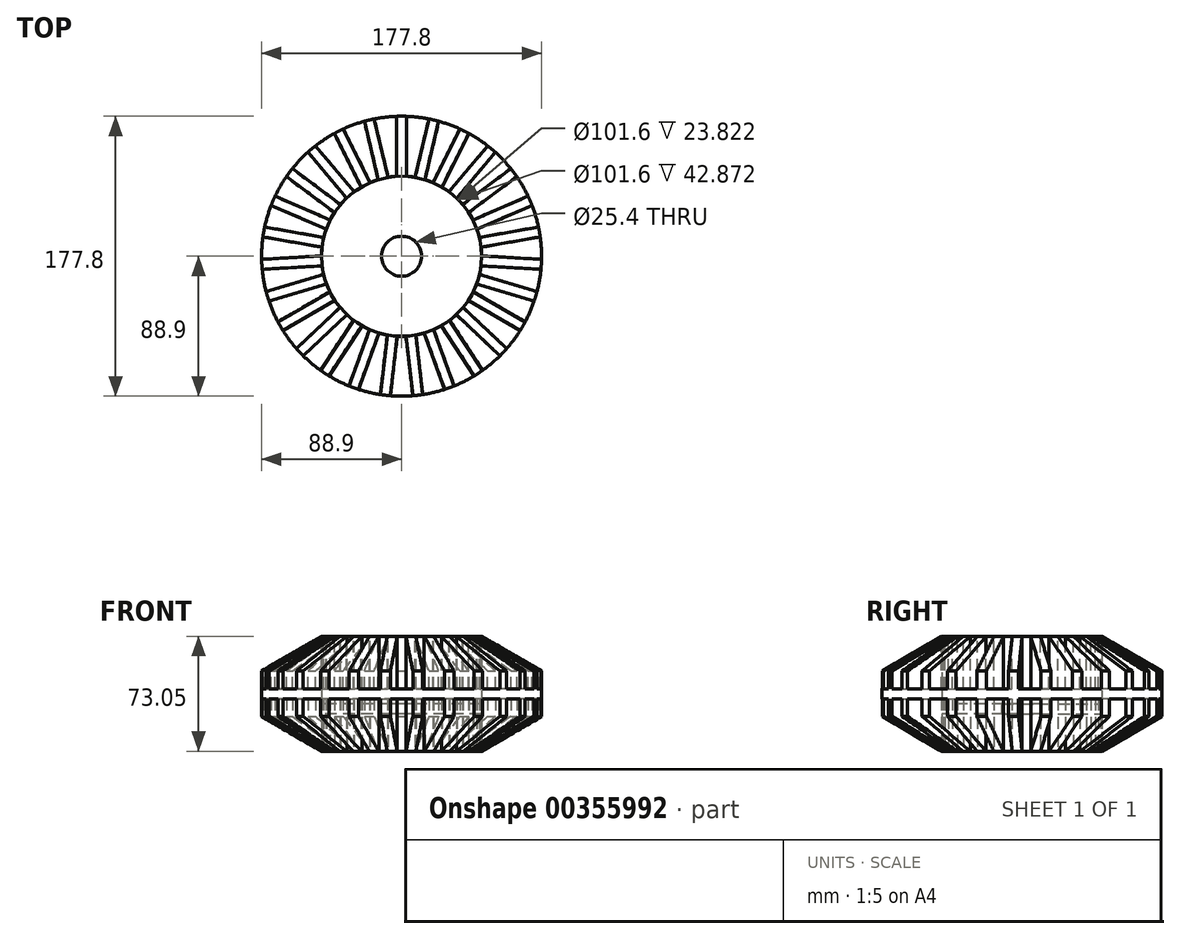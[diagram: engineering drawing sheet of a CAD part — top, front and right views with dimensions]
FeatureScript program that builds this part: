
annotation { "Feature Type Name" : "Feature", "Feature Type Description" : "" }
export const myFeature = defineFeature(function(context is Context, id is Id, definition is map)
    precondition{}
    {
        {
            var Q0;
            Q0=qCreatedBy(makeId("Top.planeOp"),FACE);
            var sketch = newSketch(context, id + "F0", { "sketchPlane" : qUnion([Q0])});
            skCircle(sketch, "E0", {"center": v(0, 0) * mm, "radius": 88.9 * mm});
            skCircle(sketch, "E1", {"center": v(0, 0) * mm, "radius": 50.8 * mm});
            skLineSegment(sketch, "E2.bottom", {"start": v(104.67, -12.7) * mm, "end": v(98.32, -12.7) * mm});
            skLineSegment(sketch, "E2.top", {"start": v(104.67, 12.7) * mm, "end": v(98.32, 12.7) * mm});
            skLineSegment(sketch, "E2.left", {"start": v(104.67, -12.7) * mm, "end": v(104.67, 12.7) * mm});
            skLineSegment(sketch, "E2.right", {"start": v(98.32, -12.7) * mm, "end": v(98.32, 12.7) * mm});
            skPoint(sketch, "E2.middle", {"position": v(101.5, 0) * mm});
            skSolve(sketch);
        }
        {
            var Q0;
            Q0=makeQuery(id+"F0.imprint","IMPRINT",FACE,{"disambiguationData":[TD([[makeQuery(id+"F0.imprint","IMPRINT",EDGE,{"derivedFrom":sQuery(id+"F0.wireOp",EDGE,"E0")}),1.0]])]});
            extrude(context, id + "F1", {"entities" : qUnion([Q0]), "depth" : 50.8 * mm});
        }
        {
            var Q0;
            Q0=makeQuery(id+"F0.imprint","IMPRINT",FACE,{"disambiguationData":[TD([[makeQuery(id+"F0.imprint","IMPRINT",EDGE,{"derivedFrom":sQuery(id+"F0.wireOp",EDGE,"E1")}),1.0]])]});
            extrude(context, id + "F2", {"entities" : qUnion([Q0]), "operationType" : NewBodyOperationType.ADD, "depth" : 6.35 * mm});
        }
        {
            var Q0;
            Q0=makeQuery(id+"F1.opExtrude","CAP_FACE",FACE,{"disambiguationData":[OSD([sQuery(id+"F0.wireOp",EDGE,"E0"),sQuery(id+"F0.wireOp",EDGE,"E1")])],"isStart":false});
            var sketch = newSketch(context, id + "F3", { "sketchPlane" : qUnion([Q0])});
            skLineSegment(sketch, "E3.0", {"start": v(-3.18, 88.9) * mm, "end": v(-3.17, 50.8) * mm});
            skLineSegment(sketch, "E4.0", {"start": v(3.18, 88.9) * mm, "end": v(3.18, 50.8) * mm});
            skPoint(sketch, "E5.start.orphan", {"position": v(0, 88.9) * mm});
            skLineSegment(sketch, "E6.1.0", {"start": v(-17.41, 87.24) * mm, "end": v(-8.63, 50.16) * mm});
            skLineSegment(sketch, "E6.1.1", {"start": v(-23.6, 85.77) * mm, "end": v(-14.8, 48.7) * mm});
            skLineSegment(sketch, "E6.2.0", {"start": v(-37.06, 80.87) * mm, "end": v(-19.96, 46.82) * mm});
            skLineSegment(sketch, "E6.2.1", {"start": v(-42.74, 78.02) * mm, "end": v(-25.64, 43.97) * mm});
            skLineSegment(sketch, "E6.3.0", {"start": v(-54.71, 70.14) * mm, "end": v(-30.22, 40.96) * mm});
            skLineSegment(sketch, "E6.3.1", {"start": v(-59.58, 66.06) * mm, "end": v(-35.09, 36.87) * mm});
            skLineSegment(sketch, "E6.4.0", {"start": v(-69.41, 55.63) * mm, "end": v(-38.85, 32.88) * mm});
            skLineSegment(sketch, "E6.4.1", {"start": v(-73.2, 50.54) * mm, "end": v(-42.64, 27.79) * mm});
            skLineSegment(sketch, "E6.5.0", {"start": v(-80.37, 38.13) * mm, "end": v(-45.39, 23.04) * mm});
            skLineSegment(sketch, "E6.5.1", {"start": v(-82.89, 32.3) * mm, "end": v(-47.9, 17.2) * mm});
            skLineSegment(sketch, "E6.6.0", {"start": v(-87, 18.56) * mm, "end": v(-49.48, 11.95) * mm});
            skLineSegment(sketch, "E6.6.1", {"start": v(-88.1, 12.31) * mm, "end": v(-50.58, 5.7) * mm});
            skLineSegment(sketch, "E6.7.0", {"start": v(-88.93, -2) * mm, "end": v(-50.9, 0.22) * mm});
            skLineSegment(sketch, "E6.7.1", {"start": v(-88.56, -8.34) * mm, "end": v(-50.53, -6.12) * mm});
            skLineSegment(sketch, "E6.8.0", {"start": v(-86.08, -22.46) * mm, "end": v(-49.58, -11.53) * mm});
            skLineSegment(sketch, "E6.8.1", {"start": v(-84.25, -28.54) * mm, "end": v(-47.76, -17.61) * mm});
            skLineSegment(sketch, "E6.9.0", {"start": v(-78.58, -41.7) * mm, "end": v(-45.58, -22.65) * mm});
            skLineSegment(sketch, "E6.9.1", {"start": v(-75.4, -47.2) * mm, "end": v(-42.4, -28.15) * mm});
            skLineSegment(sketch, "E6.10.0", {"start": v(-66.84, -58.7) * mm, "end": v(-39.13, -32.55) * mm});
            skLineSegment(sketch, "E6.10.1", {"start": v(-62.48, -63.32) * mm, "end": v(-34.77, -37.17) * mm});
            skLineSegment(sketch, "E6.11.0", {"start": v(-51.5, -72.53) * mm, "end": v(-30.57, -40.7) * mm});
            skLineSegment(sketch, "E6.11.1", {"start": v(-46.2, -76.02) * mm, "end": v(-25.26, -44.19) * mm});
            skLineSegment(sketch, "E6.12.0", {"start": v(-33.39, -82.45) * mm, "end": v(-20.36, -46.65) * mm});
            skLineSegment(sketch, "E6.12.1", {"start": v(-27.42, -84.62) * mm, "end": v(-14.4, -48.82) * mm});
            skLineSegment(sketch, "E6.13.0", {"start": v(-13.47, -87.93) * mm, "end": v(-9.05, -50.09) * mm});
            skLineSegment(sketch, "E6.13.1", {"start": v(-7.17, -88.67) * mm, "end": v(-2.74, -50.83) * mm});
            skLineSegment(sketch, "E6.14.0", {"start": v(7.17, -88.67) * mm, "end": v(2.74, -50.83) * mm});
            skLineSegment(sketch, "E6.14.1", {"start": v(13.47, -87.93) * mm, "end": v(9.05, -50.09) * mm});
            skLineSegment(sketch, "E6.15.0", {"start": v(27.42, -84.62) * mm, "end": v(14.4, -48.82) * mm});
            skLineSegment(sketch, "E6.15.1", {"start": v(33.39, -82.45) * mm, "end": v(20.36, -46.65) * mm});
            skLineSegment(sketch, "E6.16.0", {"start": v(46.2, -76.02) * mm, "end": v(25.26, -44.19) * mm});
            skLineSegment(sketch, "E6.16.1", {"start": v(51.5, -72.53) * mm, "end": v(30.57, -40.7) * mm});
            skLineSegment(sketch, "E6.17.0", {"start": v(62.48, -63.32) * mm, "end": v(34.77, -37.17) * mm});
            skLineSegment(sketch, "E6.17.1", {"start": v(66.84, -58.7) * mm, "end": v(39.13, -32.55) * mm});
            skLineSegment(sketch, "E6.18.0", {"start": v(75.4, -47.2) * mm, "end": v(42.4, -28.15) * mm});
            skLineSegment(sketch, "E6.18.1", {"start": v(78.58, -41.7) * mm, "end": v(45.58, -22.65) * mm});
            skLineSegment(sketch, "E6.19.0", {"start": v(84.25, -28.54) * mm, "end": v(47.76, -17.61) * mm});
            skLineSegment(sketch, "E6.19.1", {"start": v(86.08, -22.46) * mm, "end": v(49.58, -11.53) * mm});
            skLineSegment(sketch, "E6.20.0", {"start": v(88.56, -8.34) * mm, "end": v(50.53, -6.12) * mm});
            skLineSegment(sketch, "E6.20.1", {"start": v(88.93, -2) * mm, "end": v(50.9, 0.22) * mm});
            skLineSegment(sketch, "E6.21.0", {"start": v(88.1, 12.31) * mm, "end": v(50.58, 5.7) * mm});
            skLineSegment(sketch, "E6.21.1", {"start": v(87, 18.56) * mm, "end": v(49.48, 11.95) * mm});
            skLineSegment(sketch, "E6.22.0", {"start": v(82.89, 32.3) * mm, "end": v(47.9, 17.2) * mm});
            skLineSegment(sketch, "E6.22.1", {"start": v(80.37, 38.13) * mm, "end": v(45.39, 23.04) * mm});
            skLineSegment(sketch, "E6.23.0", {"start": v(73.2, 50.54) * mm, "end": v(42.64, 27.79) * mm});
            skLineSegment(sketch, "E6.23.1", {"start": v(69.41, 55.63) * mm, "end": v(38.85, 32.88) * mm});
            skLineSegment(sketch, "E6.24.0", {"start": v(59.58, 66.06) * mm, "end": v(35.09, 36.87) * mm});
            skLineSegment(sketch, "E6.24.1", {"start": v(54.71, 70.14) * mm, "end": v(30.22, 40.96) * mm});
            skLineSegment(sketch, "E6.25.0", {"start": v(42.74, 78.02) * mm, "end": v(25.64, 43.97) * mm});
            skLineSegment(sketch, "E6.25.1", {"start": v(37.06, 80.87) * mm, "end": v(19.96, 46.82) * mm});
            skLineSegment(sketch, "E6.26.0", {"start": v(23.6, 85.77) * mm, "end": v(14.8, 48.7) * mm});
            skLineSegment(sketch, "E6.26.1", {"start": v(17.41, 87.24) * mm, "end": v(8.63, 50.16) * mm});
            skPoint(sketch, "E6.center", {"position": v(0, 0) * mm});
            skCircle(sketch, "E7", {"center": v(0, 0) * mm, "radius": 50.9 * mm});
            skCircle(sketch, "E8", {"center": v(0, 0) * mm, "radius": 88.96 * mm});
            skSolve(sketch);
        }
        {
            var Q0;
            {var subQ0=sQuery(id+"F3.wireOp",EDGE,"E7");var subQ1=sQuery(id+"F3.wireOp",EDGE,"E6.24.1");var subQ2=makeQuery(id+"F3.imprint","INTERSECT",VERTEX,{"derivedFrom":[subQ1,subQ0]});Q0=makeQuery(id+"F3.imprint","IMPRINT",FACE,{"disambiguationData":[TD([[makeQuery(id+"F3.imprint","IMPRINT",EDGE,{"disambiguationData":[TD([[subQ2,1.0]])],"derivedFrom":subQ1}),-1.0]])]});}
            var Q1;
            {var subQ0=sQuery(id+"F3.wireOp",EDGE,"E7");var subQ1=sQuery(id+"F3.wireOp",EDGE,"E6.25.1");var subQ2=makeQuery(id+"F3.imprint","INTERSECT",VERTEX,{"derivedFrom":[subQ1,subQ0]});Q1=makeQuery(id+"F3.imprint","IMPRINT",FACE,{"disambiguationData":[TD([[makeQuery(id+"F3.imprint","IMPRINT",EDGE,{"disambiguationData":[TD([[subQ2,1.0]])],"derivedFrom":subQ1}),-1.0]])]});}
            var Q2;
            {var subQ0=sQuery(id+"F3.wireOp",EDGE,"E7");var subQ1=sQuery(id+"F3.wireOp",EDGE,"E4.0");var subQ2=makeQuery(id+"F3.imprint","INTERSECT",VERTEX,{"derivedFrom":[subQ1,subQ0]});Q2=makeQuery(id+"F3.imprint","IMPRINT",FACE,{"disambiguationData":[TD([[makeQuery(id+"F3.imprint","IMPRINT",EDGE,{"disambiguationData":[TD([[subQ2,1.0]])],"derivedFrom":subQ1}),1.0]])]});}
            var Q3;
            {var subQ0=sQuery(id+"F3.wireOp",EDGE,"E7");var subQ1=sQuery(id+"F3.wireOp",EDGE,"E3.0");var subQ2=makeQuery(id+"F3.imprint","INTERSECT",VERTEX,{"derivedFrom":[subQ1,subQ0]});Q3=makeQuery(id+"F3.imprint","IMPRINT",FACE,{"disambiguationData":[TD([[makeQuery(id+"F3.imprint","IMPRINT",EDGE,{"disambiguationData":[TD([[subQ2,1.0]])],"derivedFrom":subQ1}),-1.0]])]});}
            var Q4;
            {var subQ0=sQuery(id+"F3.wireOp",EDGE,"E7");var subQ1=sQuery(id+"F3.wireOp",EDGE,"E6.1.1");var subQ2=makeQuery(id+"F3.imprint","INTERSECT",VERTEX,{"derivedFrom":[subQ1,subQ0]});Q4=makeQuery(id+"F3.imprint","IMPRINT",FACE,{"disambiguationData":[TD([[makeQuery(id+"F3.imprint","IMPRINT",EDGE,{"disambiguationData":[TD([[subQ2,1.0]])],"derivedFrom":subQ1}),-1.0]])]});}
            var Q5;
            {var subQ0=sQuery(id+"F3.wireOp",EDGE,"E7");var subQ1=sQuery(id+"F3.wireOp",EDGE,"E6.2.1");var subQ2=makeQuery(id+"F3.imprint","INTERSECT",VERTEX,{"derivedFrom":[subQ1,subQ0]});Q5=makeQuery(id+"F3.imprint","IMPRINT",FACE,{"disambiguationData":[TD([[makeQuery(id+"F3.imprint","IMPRINT",EDGE,{"disambiguationData":[TD([[subQ2,1.0]])],"derivedFrom":subQ1}),-1.0]])]});}
            var Q6;
            {var subQ0=sQuery(id+"F3.wireOp",EDGE,"E7");var subQ1=sQuery(id+"F3.wireOp",EDGE,"E6.3.1");var subQ2=makeQuery(id+"F3.imprint","INTERSECT",VERTEX,{"derivedFrom":[subQ1,subQ0]});Q6=makeQuery(id+"F3.imprint","IMPRINT",FACE,{"disambiguationData":[TD([[makeQuery(id+"F3.imprint","IMPRINT",EDGE,{"disambiguationData":[TD([[subQ2,1.0]])],"derivedFrom":subQ1}),-1.0]])]});}
            var Q7;
            {var subQ0=sQuery(id+"F3.wireOp",EDGE,"E7");var subQ1=sQuery(id+"F3.wireOp",EDGE,"E6.4.1");var subQ2=makeQuery(id+"F3.imprint","INTERSECT",VERTEX,{"derivedFrom":[subQ1,subQ0]});Q7=makeQuery(id+"F3.imprint","IMPRINT",FACE,{"disambiguationData":[TD([[makeQuery(id+"F3.imprint","IMPRINT",EDGE,{"disambiguationData":[TD([[subQ2,1.0]])],"derivedFrom":subQ1}),-1.0]])]});}
            var Q8;
            {var subQ0=sQuery(id+"F3.wireOp",EDGE,"E7");var subQ1=sQuery(id+"F3.wireOp",EDGE,"E6.5.1");var subQ2=makeQuery(id+"F3.imprint","INTERSECT",VERTEX,{"derivedFrom":[subQ1,subQ0]});Q8=makeQuery(id+"F3.imprint","IMPRINT",FACE,{"disambiguationData":[TD([[makeQuery(id+"F3.imprint","IMPRINT",EDGE,{"disambiguationData":[TD([[subQ2,1.0]])],"derivedFrom":subQ1}),-1.0]])]});}
            var Q9;
            {var subQ0=sQuery(id+"F3.wireOp",EDGE,"E7");var subQ1=sQuery(id+"F3.wireOp",EDGE,"E6.6.1");var subQ2=makeQuery(id+"F3.imprint","INTERSECT",VERTEX,{"derivedFrom":[subQ1,subQ0]});Q9=makeQuery(id+"F3.imprint","IMPRINT",FACE,{"disambiguationData":[TD([[makeQuery(id+"F3.imprint","IMPRINT",EDGE,{"disambiguationData":[TD([[subQ2,1.0]])],"derivedFrom":subQ1}),-1.0]])]});}
            var Q10;
            {var subQ0=sQuery(id+"F3.wireOp",EDGE,"E7");var subQ1=sQuery(id+"F3.wireOp",EDGE,"E6.7.1");var subQ2=makeQuery(id+"F3.imprint","INTERSECT",VERTEX,{"derivedFrom":[subQ1,subQ0]});Q10=makeQuery(id+"F3.imprint","IMPRINT",FACE,{"disambiguationData":[TD([[makeQuery(id+"F3.imprint","IMPRINT",EDGE,{"disambiguationData":[TD([[subQ2,1.0]])],"derivedFrom":subQ1}),-1.0]])]});}
            var Q11;
            {var subQ0=sQuery(id+"F3.wireOp",EDGE,"E7");var subQ1=sQuery(id+"F3.wireOp",EDGE,"E6.8.1");var subQ2=makeQuery(id+"F3.imprint","INTERSECT",VERTEX,{"derivedFrom":[subQ1,subQ0]});Q11=makeQuery(id+"F3.imprint","IMPRINT",FACE,{"disambiguationData":[TD([[makeQuery(id+"F3.imprint","IMPRINT",EDGE,{"disambiguationData":[TD([[subQ2,1.0]])],"derivedFrom":subQ1}),-1.0]])]});}
            var Q12;
            {var subQ0=sQuery(id+"F3.wireOp",EDGE,"E7");var subQ1=sQuery(id+"F3.wireOp",EDGE,"E6.9.1");var subQ2=makeQuery(id+"F3.imprint","INTERSECT",VERTEX,{"derivedFrom":[subQ1,subQ0]});Q12=makeQuery(id+"F3.imprint","IMPRINT",FACE,{"disambiguationData":[TD([[makeQuery(id+"F3.imprint","IMPRINT",EDGE,{"disambiguationData":[TD([[subQ2,1.0]])],"derivedFrom":subQ1}),-1.0]])]});}
            var Q13;
            {var subQ0=sQuery(id+"F3.wireOp",EDGE,"E7");var subQ1=sQuery(id+"F3.wireOp",EDGE,"E6.10.1");var subQ2=makeQuery(id+"F3.imprint","INTERSECT",VERTEX,{"derivedFrom":[subQ1,subQ0]});Q13=makeQuery(id+"F3.imprint","IMPRINT",FACE,{"disambiguationData":[TD([[makeQuery(id+"F3.imprint","IMPRINT",EDGE,{"disambiguationData":[TD([[subQ2,1.0]])],"derivedFrom":subQ1}),-1.0]])]});}
            var Q14;
            {var subQ0=sQuery(id+"F3.wireOp",EDGE,"E7");var subQ1=sQuery(id+"F3.wireOp",EDGE,"E6.11.1");var subQ2=makeQuery(id+"F3.imprint","INTERSECT",VERTEX,{"derivedFrom":[subQ1,subQ0]});Q14=makeQuery(id+"F3.imprint","IMPRINT",FACE,{"disambiguationData":[TD([[makeQuery(id+"F3.imprint","IMPRINT",EDGE,{"disambiguationData":[TD([[subQ2,1.0]])],"derivedFrom":subQ1}),-1.0]])]});}
            var Q15;
            {var subQ0=sQuery(id+"F3.wireOp",EDGE,"E7");var subQ1=sQuery(id+"F3.wireOp",EDGE,"E6.12.1");var subQ2=makeQuery(id+"F3.imprint","INTERSECT",VERTEX,{"derivedFrom":[subQ1,subQ0]});Q15=makeQuery(id+"F3.imprint","IMPRINT",FACE,{"disambiguationData":[TD([[makeQuery(id+"F3.imprint","IMPRINT",EDGE,{"disambiguationData":[TD([[subQ2,1.0]])],"derivedFrom":subQ1}),-1.0]])]});}
            var Q16;
            {var subQ0=sQuery(id+"F3.wireOp",EDGE,"E7");var subQ1=sQuery(id+"F3.wireOp",EDGE,"E6.13.1");var subQ2=makeQuery(id+"F3.imprint","INTERSECT",VERTEX,{"derivedFrom":[subQ1,subQ0]});Q16=makeQuery(id+"F3.imprint","IMPRINT",FACE,{"disambiguationData":[TD([[makeQuery(id+"F3.imprint","IMPRINT",EDGE,{"disambiguationData":[TD([[subQ2,1.0]])],"derivedFrom":subQ1}),-1.0]])]});}
            var Q17;
            {var subQ0=sQuery(id+"F3.wireOp",EDGE,"E7");var subQ1=sQuery(id+"F3.wireOp",EDGE,"E6.14.1");var subQ2=makeQuery(id+"F3.imprint","INTERSECT",VERTEX,{"derivedFrom":[subQ1,subQ0]});Q17=makeQuery(id+"F3.imprint","IMPRINT",FACE,{"disambiguationData":[TD([[makeQuery(id+"F3.imprint","IMPRINT",EDGE,{"disambiguationData":[TD([[subQ2,1.0]])],"derivedFrom":subQ1}),-1.0]])]});}
            var Q18;
            {var subQ0=sQuery(id+"F3.wireOp",EDGE,"E7");var subQ1=sQuery(id+"F3.wireOp",EDGE,"E6.15.1");var subQ2=makeQuery(id+"F3.imprint","INTERSECT",VERTEX,{"derivedFrom":[subQ1,subQ0]});Q18=makeQuery(id+"F3.imprint","IMPRINT",FACE,{"disambiguationData":[TD([[makeQuery(id+"F3.imprint","IMPRINT",EDGE,{"disambiguationData":[TD([[subQ2,1.0]])],"derivedFrom":subQ1}),-1.0]])]});}
            var Q19;
            {var subQ0=sQuery(id+"F3.wireOp",EDGE,"E7");var subQ1=sQuery(id+"F3.wireOp",EDGE,"E6.16.1");var subQ2=makeQuery(id+"F3.imprint","INTERSECT",VERTEX,{"derivedFrom":[subQ1,subQ0]});Q19=makeQuery(id+"F3.imprint","IMPRINT",FACE,{"disambiguationData":[TD([[makeQuery(id+"F3.imprint","IMPRINT",EDGE,{"disambiguationData":[TD([[subQ2,1.0]])],"derivedFrom":subQ1}),-1.0]])]});}
            var Q20;
            {var subQ0=sQuery(id+"F3.wireOp",EDGE,"E7");var subQ1=sQuery(id+"F3.wireOp",EDGE,"E6.17.1");var subQ2=makeQuery(id+"F3.imprint","INTERSECT",VERTEX,{"derivedFrom":[subQ1,subQ0]});Q20=makeQuery(id+"F3.imprint","IMPRINT",FACE,{"disambiguationData":[TD([[makeQuery(id+"F3.imprint","IMPRINT",EDGE,{"disambiguationData":[TD([[subQ2,1.0]])],"derivedFrom":subQ1}),-1.0]])]});}
            var Q21;
            {var subQ0=sQuery(id+"F3.wireOp",EDGE,"E7");var subQ1=sQuery(id+"F3.wireOp",EDGE,"E6.18.1");var subQ2=makeQuery(id+"F3.imprint","INTERSECT",VERTEX,{"derivedFrom":[subQ1,subQ0]});Q21=makeQuery(id+"F3.imprint","IMPRINT",FACE,{"disambiguationData":[TD([[makeQuery(id+"F3.imprint","IMPRINT",EDGE,{"disambiguationData":[TD([[subQ2,1.0]])],"derivedFrom":subQ1}),-1.0]])]});}
            var Q22;
            {var subQ0=sQuery(id+"F3.wireOp",EDGE,"E7");var subQ1=sQuery(id+"F3.wireOp",EDGE,"E6.19.1");var subQ2=makeQuery(id+"F3.imprint","INTERSECT",VERTEX,{"derivedFrom":[subQ1,subQ0]});Q22=makeQuery(id+"F3.imprint","IMPRINT",FACE,{"disambiguationData":[TD([[makeQuery(id+"F3.imprint","IMPRINT",EDGE,{"disambiguationData":[TD([[subQ2,1.0]])],"derivedFrom":subQ1}),-1.0]])]});}
            var Q23;
            {var subQ0=sQuery(id+"F3.wireOp",EDGE,"E7");var subQ1=sQuery(id+"F3.wireOp",EDGE,"E6.20.1");var subQ2=makeQuery(id+"F3.imprint","INTERSECT",VERTEX,{"derivedFrom":[subQ1,subQ0]});Q23=makeQuery(id+"F3.imprint","IMPRINT",FACE,{"disambiguationData":[TD([[makeQuery(id+"F3.imprint","IMPRINT",EDGE,{"disambiguationData":[TD([[subQ2,1.0]])],"derivedFrom":subQ1}),-1.0]])]});}
            var Q24;
            {var subQ0=sQuery(id+"F3.wireOp",EDGE,"E7");var subQ1=sQuery(id+"F3.wireOp",EDGE,"E6.21.1");var subQ2=makeQuery(id+"F3.imprint","INTERSECT",VERTEX,{"derivedFrom":[subQ1,subQ0]});Q24=makeQuery(id+"F3.imprint","IMPRINT",FACE,{"disambiguationData":[TD([[makeQuery(id+"F3.imprint","IMPRINT",EDGE,{"disambiguationData":[TD([[subQ2,1.0]])],"derivedFrom":subQ1}),-1.0]])]});}
            var Q25;
            {var subQ0=sQuery(id+"F3.wireOp",EDGE,"E7");var subQ1=sQuery(id+"F3.wireOp",EDGE,"E6.22.1");var subQ2=makeQuery(id+"F3.imprint","INTERSECT",VERTEX,{"derivedFrom":[subQ1,subQ0]});Q25=makeQuery(id+"F3.imprint","IMPRINT",FACE,{"disambiguationData":[TD([[makeQuery(id+"F3.imprint","IMPRINT",EDGE,{"disambiguationData":[TD([[subQ2,1.0]])],"derivedFrom":subQ1}),-1.0]])]});}
            var Q26;
            {var subQ0=sQuery(id+"F3.wireOp",EDGE,"E7");var subQ1=sQuery(id+"F3.wireOp",EDGE,"E6.23.1");var subQ2=makeQuery(id+"F3.imprint","INTERSECT",VERTEX,{"derivedFrom":[subQ1,subQ0]});Q26=makeQuery(id+"F3.imprint","IMPRINT",FACE,{"disambiguationData":[TD([[makeQuery(id+"F3.imprint","IMPRINT",EDGE,{"disambiguationData":[TD([[subQ2,1.0]])],"derivedFrom":subQ1}),-1.0]])]});}
            var Q27;
            Q27=makeQuery(id+"F3.imprint","IMPRINT",FACE,{"disambiguationData":[TD([[makeQuery(id+"F3.imprint","IMPRINT",EDGE,{"derivedFrom":makeQuery(id+"F1.opExtrude","CAP_EDGE",EDGE,{"disambiguationData":[OSD([sQuery(id+"F0.wireOp",EDGE,"E1")])],"isStart":false})}),1.0]])]});
            extrude(context, id + "F4", {"entities" : qUnion([Q0, Q1, Q2, Q3, Q4, Q5, Q6, Q7, Q8, Q9, Q10, Q11, Q12, Q13, Q14, Q15, Q16, Q17, Q18, Q19, Q20, Q21, Q22, Q23, Q24, Q25, Q26, Q27]), "operationType" : NewBodyOperationType.REMOVE, "oppositeDirection" : true, "depth" : 38.1 * mm});
        }
        {
            var Q0;
            Q0=qCreatedBy(makeId("Front.planeOp"),FACE);
            var sketch = newSketch(context, id + "F5", { "sketchPlane" : qUnion([Q0])});
            skLineSegment(sketch, "E9", {"start": v(89.9, 0) * mm, "end": v(89.9, 23.48) * mm});
            skLineSegment(sketch, "E10", {"start": v(89.9, 23.48) * mm, "end": v(41.8, 51.25) * mm});
            skLineSegment(sketch, "E11", {"start": v(41.8, 51.25) * mm, "end": v(107.98, 74.03) * mm});
            skLineSegment(sketch, "E12", {"start": v(107.98, 74.03) * mm, "end": v(154.62, -12.88) * mm});
            skLineSegment(sketch, "E13", {"start": v(154.62, -12.88) * mm, "end": v(91.48, -12.88) * mm});
            skLineSegment(sketch, "E14", {"start": v(91.48, -12.88) * mm, "end": v(89.9, 0) * mm});
            skSolve(sketch);
        }
        {
            var Q0;
            Q0=qSketchRegion(id+"F5",true);
            var Q1;
            Q1=makeQuery(id+"F1.opExtrude","CAP_EDGE",EDGE,{"disambiguationData":[OSD([sQuery(id+"F0.wireOp",EDGE,"E0")])],"isStart":true});
            revolve(context, id + "F6", {"operationType" : NewBodyOperationType.REMOVE, "entities" : qUnion([Q0]), "axis" : qUnion([Q1]), "revolveType" : RevolveType.FULL, "oppositeDirection" : true});
        }
        {
            var Q0;
            Q0=makeQuery(id+"F2.opExtrude","CAP_FACE",FACE,{"disambiguationData":[OSD([sQuery(id+"F0.wireOp",EDGE,"E1")])],"isStart":false});
            var sketch = newSketch(context, id + "F7", { "sketchPlane" : qUnion([Q0])});
            skCircle(sketch, "E15", {"center": v(0, 0) * mm, "radius": 12.7 * mm});
            skSolve(sketch);
        }
        {
            var Q0;
            Q0=makeQuery(id+"F7.imprint","IMPRINT",FACE,{"disambiguationData":[TD([[makeQuery(id+"F7.imprint","IMPRINT",EDGE,{"derivedFrom":sQuery(id+"F7.wireOp",EDGE,"E15")}),1.0]])]});
            extrude(context, id + "F8", {"entities" : qUnion([Q0]), "operationType" : NewBodyOperationType.REMOVE, "oppositeDirection" : true, "depth" : 25.4 * mm});
        }
        {
            var Q0;
            {var subQ0=sQuery(id+"F0.wireOp",EDGE,"E1");Q0=makeQuery(id+"F2.boolean.opBoolean","MERGE",FACE,{"derivedFrom":[makeQuery(id+"F1.opExtrude","CAP_FACE",FACE,{"disambiguationData":[OSD([sQuery(id+"F0.wireOp",EDGE,"E0"),subQ0])],"isStart":true}),makeQuery(id+"F2.opExtrude","CAP_FACE",FACE,{"disambiguationData":[OSD([subQ0])],"isStart":true})]});}
            extrude(context, id + "F9", {"entities" : qUnion([Q0]), "operationType" : NewBodyOperationType.REMOVE, "oppositeDirection" : true, "depth" : 9.52 * mm});
        }
        {
            var Q0;
            Q0=makeQuery(id+"F1.opExtrude","SWEPT_BODY",BODY,{"disambiguationData":[OSD([sQuery(id+"F0.wireOp",EDGE,"E0"),sQuery(id+"F0.wireOp",EDGE,"E1")])]});
            var Q1;
            Q1=makeQuery(id+"F9.boolean.opBoolean","COPY",FACE,{"derivedFrom":makeQuery(id+"F9.opExtrude","CAP_FACE",FACE,{"disambiguationData":[OSD([sQuery(id+"F0.wireOp",EDGE,"E0"),sQuery(id+"F0.wireOp",EDGE,"E1")])],"isStart":false})});
            mirror(context, id + "F10", {"operationType" : NewBodyOperationType.ADD, "entities" : qUnion([Q0]), "mirrorPlane" : qUnion([Q1])});
        }
        {
            var Q0;
            Q0=qCreatedBy(makeId("Top.planeOp"),FACE);
            var sketch = newSketch(context, id + "F11", { "sketchPlane" : qUnion([Q0])});
            skCircle(sketch, "E16", {"center": v(0, 0) * mm, "radius": 50.8 * mm});
            skSolve(sketch);
        }
        {
            var Q0;
            Q0=qSketchRegion(id+"F11",true);
            extrude(context, id + "F12", {"entities" : qUnion([Q0]), "operationType" : NewBodyOperationType.ADD, "endBound" : BoundingType.SYMMETRIC, "depth" : 6.35 * mm});
        }
        {
            var Q0;
            Q0=makeQuery(id+"F12.opExtrude","CAP_FACE",FACE,{"disambiguationData":[OSD([sQuery(id+"F11.wireOp",EDGE,"E16")])],"isStart":false});
            var sketch = newSketch(context, id + "F13", { "sketchPlane" : qUnion([Q0])});
            skCircle(sketch, "E17", {"center": v(0, 0) * mm, "radius": 12.7 * mm});
            skSolve(sketch);
        }
        {
            var Q0;
            Q0=makeQuery(id+"F13.imprint","IMPRINT",FACE,{"disambiguationData":[TD([[makeQuery(id+"F13.imprint","IMPRINT",EDGE,{"derivedFrom":sQuery(id+"F13.wireOp",EDGE,"E17")}),1.0]])]});
            extrude(context, id + "F14", {"entities" : qUnion([Q0]), "operationType" : NewBodyOperationType.REMOVE, "oppositeDirection" : true, "depth" : 25.4 * mm});
        }
    });
